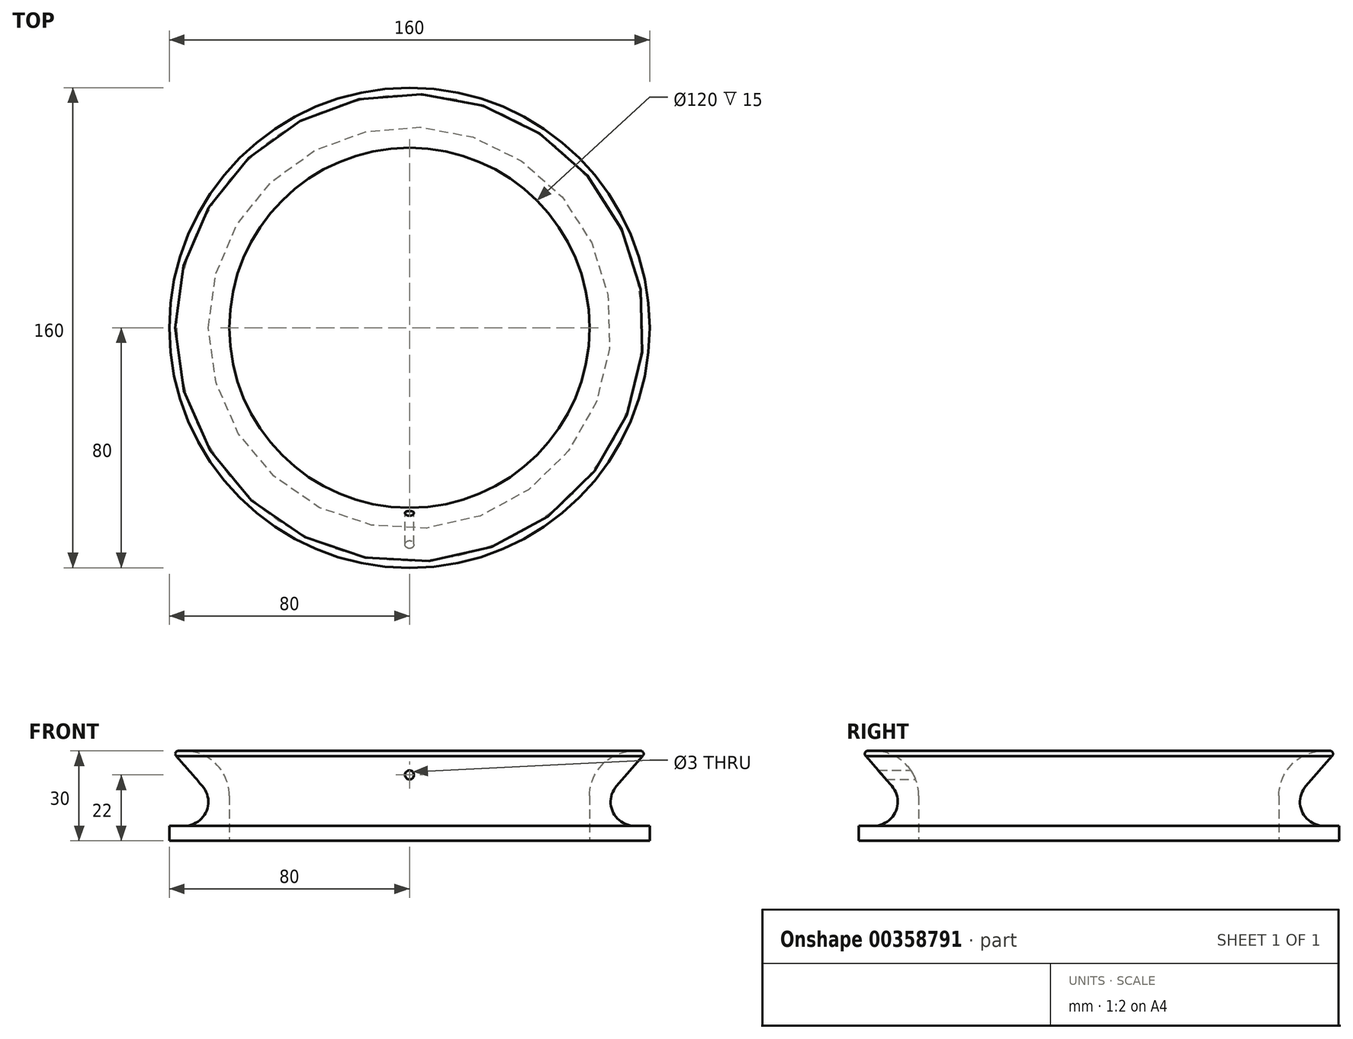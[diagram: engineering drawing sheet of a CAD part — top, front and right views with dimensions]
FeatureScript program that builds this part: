
annotation { "Feature Type Name" : "Feature", "Feature Type Description" : "" }
export const myFeature = defineFeature(function(context is Context, id is Id, definition is map)
    precondition{}
    {
        {
            var Q0;
            Q0=qCreatedBy(makeId("Front.planeOp"),FACE);
            var sketch = newSketch(context, id + "F0", { "sketchPlane" : qUnion([Q0])});
            skLineSegment(sketch, "E0", {"start": v(-80, 0) * mm, "end": v(-60, 0) * mm});
            skLineSegment(sketch, "E1", {"start": v(-60, 0) * mm, "end": v(-60, 15) * mm});
            skLineSegment(sketch, "E2", {"start": v(-75, 30) * mm, "end": v(-77, 30) * mm});
            skLineSegment(sketch, "E3", {"start": v(-75, 5) * mm, "end": v(-80, 5) * mm});
            skLineSegment(sketch, "E4", {"start": v(-80, 5) * mm, "end": v(-80, 0) * mm});
            skPoint(sketch, "E5.visualSharp", {"position": v(-60, 30) * mm});
            skArc(sketch, "E5.filletArc", {"start": v(-60, 15) * mm, "mid": v(-64.4, 25.6) * mm, "end": v(-75, 30) * mm});
            skArc(sketch, "E6.filletArc", {"start": v(-75, 5) * mm, "mid": v(-67.7, 9.7) * mm, "end": v(-69, 18.3) * mm});
            skArc(sketch, "E7.filletArc", {"start": v(-77, 30) * mm, "mid": v(-77.95, 29.32) * mm, "end": v(-77.6, 28.2) * mm});
            skLineSegment(sketch, "E8", {"start": v(-77.6, 28.2) * mm, "end": v(-69, 18.3) * mm});
            skSolve(sketch);
        }
        {
            var Q0;
            Q0=qCreatedBy(makeId("Front.planeOp"),FACE);
            var sketch = newSketch(context, id + "F1", { "sketchPlane" : qUnion([Q0])});
            skLineSegment(sketch, "E9", {"start": v(0, 10.68) * mm, "end": v(0, 46.4) * mm});
            skSolve(sketch);
        }
        {
            var Q0;
            Q0=makeQuery(id+"F0.imprint","IMPRINT",FACE,{"disambiguationData":[TD([[makeQuery(id+"F0.imprint","IMPRINT",EDGE,{"derivedFrom":sQuery(id+"F0.wireOp",EDGE,"E0")}),1.0]])]});
            var Q1;
            Q1=sQuery(id+"F1.wireOp",EDGE,"E9");
            revolve(context, id + "F2", {"entities" : qUnion([Q0]), "axis" : qUnion([Q1]), "revolveType" : RevolveType.FULL});
        }
        {
            var Q0;
            Q0=qCreatedBy(makeId("Front.planeOp"),FACE);
            var sketch = newSketch(context, id + "F3", { "sketchPlane" : qUnion([Q0])});
            skCircle(sketch, "E10", {"center": v(0, 22) * mm, "radius": 1.5 * mm});
            skSolve(sketch);
        }
        {
            var Q0;
            Q0 = qSketchRegion(id + "F3", true);
            extrude(context, id + "F4", {"entities" : qUnion([Q0]), "operationType" : NewBodyOperationType.REMOVE, "endBound" : BoundingType.THROUGH_ALL, "depth" : 25 * mm});
        }
    });
